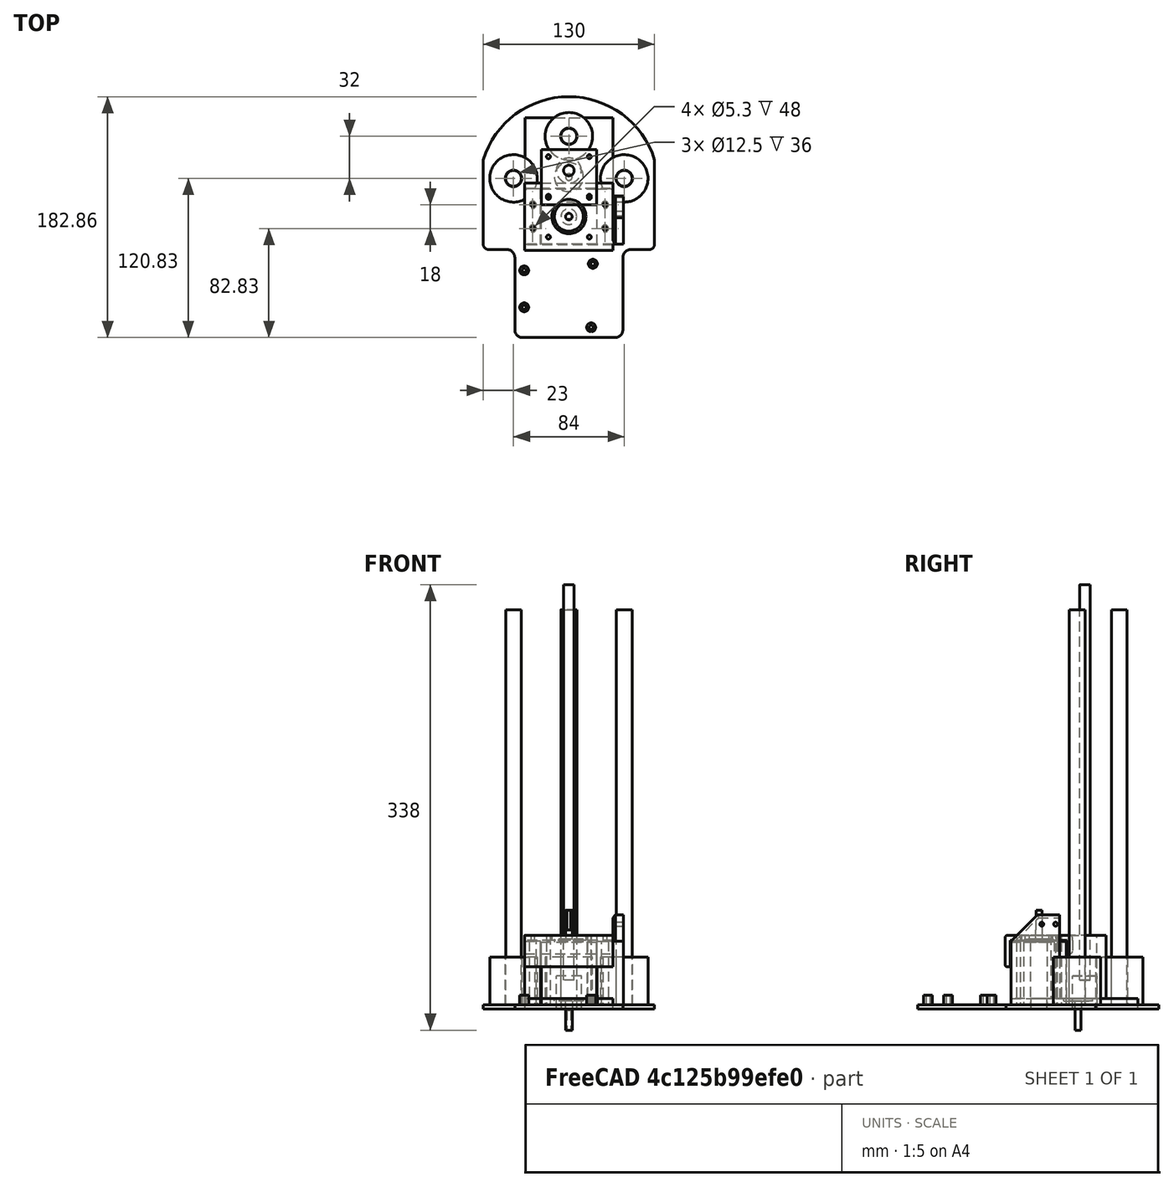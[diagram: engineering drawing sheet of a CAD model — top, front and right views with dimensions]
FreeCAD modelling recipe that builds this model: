
FCSTD DOCUMENT  (FreeCAD 0.18R16110 (Git))
Label: jSCARA-V3
License: All rights reserved
LicenseURL: http://en.wikipedia.org/wiki/All_rights_reserved
objects: PartDesign::Pad×15, Sketcher::SketchObject×10, Part::Cylinder×5, PartDesign::Fillet×4, PartDesign::Body×3, App::Part×3, PartDesign::Mirrored×2, Part::FeaturePython×2, Mesh::Feature×2, PartDesign::Chamfer×2, PartDesign::Pocket×1
note: 60 computed .brp shape members not serialized (recipe doc carries the construction recipe); baked Part::Feature solids carry a one-line shape summary decoded from their .brp

FEATURE [Sketcher::SketchObject] Sketch
  MapMode = 5
  Support = -> [XY_Plane]
  sketch-geometry (6):
    g0: LineSegment StartX=-65 StartY=-1.5e-15 StartZ=0 EndX=-65 EndY=-60 EndZ=0
    g1: LineSegment StartX=-65 StartY=-60 StartZ=0 EndX=65 EndY=-60 EndZ=0
    g2: LineSegment StartX=65 StartY=-60 StartZ=0 EndX=65 EndY=0 EndZ=0
    g3: ArcOfCircle CenterX=-1.086e-13 CenterY=-11.975 CenterZ=0 NormalX=0 NormalY=0 NormalZ=1 AngleXU=0 Radius=68 StartAngle=0.298147 EndAngle=2.84345
    g4: LineSegment StartX=65 StartY=8 StartZ=0 EndX=65 EndY=0 EndZ=0
    g5: LineSegment StartX=-65 StartY=-1.5e-15 StartZ=0 EndX=-65 EndY=8 EndZ=0
  constraints (18):
    c: Coincident(g0,g1)
    c: Coincident(g1,g2)
    c: Vertical(g2)
    c: Vertical(g0)
    c: Symmetric(g1,g0,g-2)
    c: DistanceX(g1,g1) = 130
    c: Equal(g0,g2)
    c: DistanceY(g2,g2) = 60
    c: Radius(g3) = 68
    c: Coincident(g4,g3)
    c: PointOnObject(g4,g-1)
    c: Vertical(g4)
    c: Coincident(g2,g4)
    c: Coincident(g5,g0)
    c: Coincident(g5,g3)
    c: Vertical(g5)
    c: Equal(g4,g5)
    c: DistanceY(g5,g5) = 8
FEATURE [PartDesign::Pad] Pad  label="Base"
  Length = 3.4
  Length2 = 100
  Profile = -> Sketch
  Type = 0
FEATURE [Part::Cylinder] Cylinder  label="R Rail"
  Angle = 360
  AttacherType = Attacher::AttachEngine3D
  Height = 300
  Placement = pos=(42,-6,3) rot=(0,0,1;0rad)
  Radius = 6
FEATURE [Sketcher::SketchObject] Sketch001
  MapMode = 5
  Placement = pos=(0,0,3.4) rot=(0,0,1;0rad)
  Support = -> [Pad]
  sketch-geometry (2):
    g0: Circle CenterX=42 CenterY=-6 CenterZ=0 NormalX=0 NormalY=0 NormalZ=1 AngleXU=0 Radius=6.25
    g1: Circle CenterX=42 CenterY=-6 CenterZ=0 NormalX=0 NormalY=0 NormalZ=1 AngleXU=0 Radius=18
  constraints (5):
    c: Radius(g0) = 6.25
    c: Coincident(g1,g0)
    c: Radius(g1) = 18
    c: DistanceY(g0,g-1) = 6
    c: DistanceX(g-1,g0) = 42
FEATURE [PartDesign::Fillet] Fillet
  Base = -> Pad [Edge5,Edge2]
  BaseFeature = -> Pad
  Radius = 4
FEATURE [PartDesign::Pad] Pad001  label="Rod Holder R"
  BaseFeature = -> Fillet
  Length = 36
  Length2 = 100
  Profile = -> Sketch001
  Type = 0
FEATURE [PartDesign::Mirrored] Mirrored  label="Rod Holder L"
  BaseFeature = -> Pad001
  MirrorPlane = -> YZ_Plane
  Originals = -> [Pad001]
FEATURE [Part::FeaturePython] b_NEMASteppper__42x48__001_  label="NEMASteppper (42x48)_001"  # a2plus imported part (geometry in sourceFile) (typed FeaturePython)
  Placement = pos=(0,-35,3) rot=(0,0,1;0rad)
  a2p_Version = V0.1
  fixedPosition = true
  sourceFile = .\NEMASteppper (42x48).FCStd
  subassemblyImport = false
  timeLastImport = 1.55797e+09
  updateColors = true
FEATURE [Part::Cylinder] Cylinder001  label="L Rail"
  Angle = 360
  AttacherType = Attacher::AttachEngine3D
  Height = 300
  Placement = pos=(-42,-6,3) rot=(0,0,1;0rad)
  Radius = 6
FEATURE [Sketcher::SketchObject] Sketch002
  MapMode = 5
  Placement = pos=(0,0,3.4) rot=(0,0,1;0rad)
  Support = -> [Mirrored]
  sketch-geometry (7):
    g0: LineSegment StartX=-21.4 StartY=-56 StartZ=0 EndX=-21.4 EndY=-14 EndZ=0
    g1: LineSegment StartX=-21.4 StartY=-14 StartZ=0 EndX=-33.4 EndY=-14 EndZ=0
    g2: LineSegment StartX=-33.4 StartY=-14 StartZ=0 EndX=-33.4 EndY=-56 EndZ=0
    g3: LineSegment StartX=-33.4 StartY=-56 StartZ=0 EndX=-21.4 EndY=-56 EndZ=0
    g4: Circle CenterX=-27.4 CenterY=-26 CenterZ=0 NormalX=0 NormalY=0 NormalZ=1 AngleXU=0 Radius=2.65
    g5: Circle CenterX=-27.4 CenterY=-44 CenterZ=0 NormalX=0 NormalY=0 NormalZ=1 AngleXU=0 Radius=2.65
    g6: LineSegment [constr] StartX=-27.4 StartY=-14 StartZ=0 EndX=-27.4 EndY=-56 EndZ=0
  constraints (21):
    c: Vertical(g0)
    c: Coincident(g0,g1)
    c: Horizontal(g1)
    c: Coincident(g1,g2)
    c: Vertical(g2)
    c: Coincident(g2,g3)
    c: Coincident(g3,g0)
    c: Horizontal(g3)
    c: DistanceY(g0,g-1) = 14
    c: DistanceY(g0,g0) = 42
    c: DistanceX(g1,g1) = 12
    c: DistanceX(g0,g-1) = 21.4
    c: DistanceY(g4,g1) = 12
    c: Equal(g4,g5) = 3
    c: PointOnObject(g6,g1)
    c: Symmetric(g0,g2,g6)
    c: PointOnObject(g5,g6)
    c: PointOnObject(g4,g6)
    c: PointOnObject(g6,g3)
    c: DistanceY(g2,g5) = 12
    c: Diameter(g4) = 5.3
FEATURE [PartDesign::Pad] Pad002
  BaseFeature = -> Mirrored
  Length = 48
  Length2 = 100
  Profile = -> Sketch002
  Type = 0
FEATURE [PartDesign::Mirrored] Mirrored001
  BaseFeature = -> Pad002
  MirrorPlane = -> Sketch002 [V_Axis]
  Originals = -> [Pad002]
FEATURE [Sketcher::SketchObject] Sketch003
  MapMode = 5
  Support = -> [XY_Plane002]
  sketch-geometry (14):
    g0: Circle CenterX=-27.4 CenterY=-26 CenterZ=0 NormalX=0 NormalY=0 NormalZ=1 AngleXU=0 Radius=1.5
    g1: Circle CenterX=0 CenterY=-35 CenterZ=0 NormalX=0 NormalY=0 NormalZ=1 AngleXU=0 Radius=13
    g2: LineSegment StartX=-33.4 StartY=-14 StartZ=0 EndX=33.4 EndY=-14 EndZ=0
    g3: LineSegment StartX=33.4 StartY=-14 StartZ=0 EndX=33.4 EndY=-56 EndZ=0
    g4: LineSegment StartX=33.4 StartY=-56 StartZ=0 EndX=-33.4 EndY=-56 EndZ=0
    g5: LineSegment StartX=-33.4 StartY=-56 StartZ=0 EndX=-33.4 EndY=-14 EndZ=0
    g6: Circle CenterX=27.4 CenterY=-26 CenterZ=0 NormalX=0 NormalY=0 NormalZ=1 AngleXU=0 Radius=1.5
    g7: Circle CenterX=27.4 CenterY=-44 CenterZ=0 NormalX=0 NormalY=0 NormalZ=1 AngleXU=0 Radius=1.5
    g8: Circle CenterX=-27.4 CenterY=-44 CenterZ=0 NormalX=0 NormalY=0 NormalZ=1 AngleXU=0 Radius=1.5
    g9: LineSegment [constr] StartX=-27.4 StartY=-26 StartZ=0 EndX=-27.4 EndY=-44 EndZ=0
    g10: Circle CenterX=-15.5 CenterY=-50.5 CenterZ=0 NormalX=0 NormalY=0 NormalZ=1 AngleXU=0 Radius=1.5
    g11: Circle CenterX=15.5 CenterY=-50.5 CenterZ=0 NormalX=0 NormalY=0 NormalZ=1 AngleXU=0 Radius=1.5
    g12: Circle CenterX=-15.5 CenterY=-19.5 CenterZ=0 NormalX=0 NormalY=0 NormalZ=1 AngleXU=0 Radius=1.5
    g13: Circle CenterX=15.5 CenterY=-19.5 CenterZ=0 NormalX=0 NormalY=0 NormalZ=1 AngleXU=0 Radius=1.5
  constraints (36):
    c: PointOnObject(g1,g-2)
    c: Radius(g1) = 13
    c: DistanceY(g1,g-1) = 35
    c: Coincident(g2,g3)
    c: Coincident(g3,g4)
    c: Coincident(g4,g5)
    c: Coincident(g5,g2)
    c: Horizontal(g4)
    c: Vertical(g3)
    c: Vertical(g5)
    c: DistanceX(g2,g2) = 66.8
    c: Symmetric(g2,g2,g-2)
    c: DistanceY(g3,g3) = 42
    c: DistanceY(g2,g-1) = 14
    c: Equal(g0,g6) = 3
    c: Symmetric(g6,g0,g-2)
    c: Equal(g0,g8) = 3
    c: Equal(g8,g7) = 3
    c: DistanceY(g1,g6) = 9
    c: DistanceY(g8,g0) = 18
    c: Symmetric(g7,g8,g-2)
    c: Coincident(g9,g0)
    c: Coincident(g9,g8)
    c: Vertical(g9)
    c: Radius(g10) = 1.5
    c: Equal(g10,g11) = 3
    c: Symmetric(g10,g11,g-2)
    c: DistanceX(g10,g11) = 31
    c: DistanceY(g3,g11) = 5.5
    c: Equal(g10,g12) = 3
    c: Symmetric(g12,g13,g-2)
    c: DistanceX(g12,g13) = 31
    c: DistanceY(g10,g12) = 31
    c: Equal(g13,g12)
    c: DistanceX(g4,g8) = 6
    c: Radius(g0) = 1.5
FEATURE [PartDesign::Pad] Pad003
  Length = 4
  Length2 = 100
  Profile = -> Sketch003
  Type = 0
FEATURE [PartDesign::Fillet] Fillet002
  Base = -> Mirrored001 [Edge43,Edge56]
  BaseFeature = -> Mirrored001
  Radius = 2
FEATURE [PartDesign::Pad] Pad004
  BaseFeature = -> Pad003
  Length = 0.6
  Length2 = 100
  Profile = -> Pad003 [Face3]
  Type = 0
FEATURE [PartDesign::Pad] Pad005
  BaseFeature = -> Pad004
  Length = 4
  Length2 = 100
  Profile = -> Pad004 [Face19]
  Type = 0
FEATURE [PartDesign::Pad] Pad006
  BaseFeature = -> Pad005
  Length = 20
  Length2 = 100
  Profile = -> Pad005 [Face21]
  Type = 0
FEATURE [PartDesign::Pad] Pad007
  BaseFeature = -> Pad006
  Length = 0.6
  Length2 = 100
  Profile = -> Pad006 [Face1]
  Type = 0
FEATURE [PartDesign::Pad] Pad008
  BaseFeature = -> Pad007
  Length = 4
  Length2 = 100
  Profile = -> Pad007 [Face11]
  Type = 0
FEATURE [PartDesign::Pad] Pad009
  BaseFeature = -> Pad008
  Length = 10
  Length2 = 100
  Profile = -> Pad008 [Face28]
  Type = 0
FEATURE [PartDesign::Fillet] Fillet003
  Base = -> Pad009 [Edge83,Edge65,Edge75,Edge87]
  BaseFeature = -> Pad009
  Radius = 2
FEATURE [PartDesign::Body] Body001  label="Stepper Retainer"
  Group = -> [Sketch003,Pad003,Pad004,Pad005,Pad006,Pad007,Pad008,Pad009,Fillet003]
  Origin = -> Origin002
  Placement = pos=(0,0,52) rot=(0,0,1;0rad)
  Tip = -> Fillet003
FEATURE [Mesh::Feature] KW12_3_Microswitch  label="KW12-3 Microswitch"
  Placement = pos=(48,-15,58) rot=(-0.57735,0.57735,0.57735;4.18879rad)
FEATURE [Part::Cylinder] Cylinder002  label="Lead Screw Coupler"
  Angle = 360
  AttacherType = Attacher::AttachEngine3D
  Height = 25
  Radius = 9.5
FEATURE [Sketcher::SketchObject] Sketch004
  ExternalGeometry = -> [Fillet002]
  MapMode = 5
  Placement = pos=(0,0,3.4) rot=(0,0,1;0rad)
  Support = -> [Fillet002]
  sketch-geometry (4):
    g0: LineSegment StartX=33.4 StartY=-19.3196 StartZ=0 EndX=41.4 EndY=-19.3196 EndZ=0
    g1: LineSegment StartX=41.4 StartY=-19.3196 StartZ=0 EndX=41.4 EndY=-56 EndZ=0
    g2: LineSegment StartX=41.4 StartY=-56 StartZ=0 EndX=33.4 EndY=-56 EndZ=0
    g3: LineSegment StartX=33.4 StartY=-56 StartZ=0 EndX=33.4 EndY=-19.3196 EndZ=0
  constraints (9):
    c: Coincident(g0,g1)
    c: Coincident(g1,g2)
    c: Coincident(g2,g3)
    c: Coincident(g3,g0)
    c: Horizontal(g0)
    c: Horizontal(g2)
    c: Vertical(g1)
    c: Vertical(g3)
    c: DistanceX(g0,g0) = 8
FEATURE [PartDesign::Pad] Pad010
  BaseFeature = -> Fillet002
  Length = 68
  Length2 = 100
  Profile = -> Sketch004
  Type = 0
FEATURE [PartDesign::Chamfer] Chamfer
  Base = -> Pad010 [Edge78]
  BaseFeature = -> Pad010
  Size = 20
FEATURE [PartDesign::Chamfer] Chamfer001
  Base = -> Chamfer [Edge12,Edge35]
  BaseFeature = -> Chamfer
  Size = 2
FEATURE [Sketcher::SketchObject] Sketch005
  MapMode = 5
  Placement = pos=(41.4,0,0) rot=(0.57735,0.57735,0.57735;2.0944rad)
  Support = -> [Chamfer001]
  sketch-geometry (3):
    g0: Circle CenterX=-32.7462 CenterY=64.4514 CenterZ=0 NormalX=0 NormalY=0 NormalZ=1 AngleXU=0 Radius=1.5
    g1: Circle CenterX=-22.2462 CenterY=64.4514 CenterZ=0 NormalX=0 NormalY=0 NormalZ=1 AngleXU=0 Radius=1.5
    g2: LineSegment [constr] StartX=-32.7462 StartY=64.4514 StartZ=0 EndX=-22.2462 EndY=64.4514 EndZ=0
  constraints (6):
    c: Radius(g0) = 1.5
    c: Horizontal(g2)
    c: Coincident(g2,g0)
    c: Coincident(g2,g1)
    c: Equal(g1,g0)
    c: DistanceX(g2,g2) = 10.5
FEATURE [PartDesign::Pocket] Pocket
  BaseFeature = -> Chamfer001
  Length = 10
  Length2 = 0
  Profile = -> Sketch005
  Type = 0
FEATURE [Part::Cylinder] Cylinder003  label="Lead Screw"
  Angle = 360
  AttacherType = Attacher::AttachEngine3D
  Height = 300
  Placement = pos=(0,0,22) rot=(0,0,1;0rad)
  Radius = 4
FEATURE [App::Part] Part001  label="Z Screw"
  Group = -> [Cylinder003,Cylinder002]
  Origin = -> Origin003
  Placement = pos=(0,-35,61) rot=(0,0,1;0rad)
FEATURE [Sketcher::SketchObject] Sketch006
  MapMode = 5
  Support = -> [XY_Plane005]
  sketch-geometry (5):
    g0: LineSegment StartX=-33.3207 StartY=40 StartZ=0 EndX=33.3207 EndY=40 EndZ=0
    g1: LineSegment StartX=33.3207 StartY=40 StartZ=0 EndX=33.3207 EndY=-56 EndZ=0
    g2: LineSegment StartX=33.3207 StartY=-56 StartZ=0 EndX=-33.3207 EndY=-56 EndZ=0
    g3: LineSegment StartX=-33.3207 StartY=-56 StartZ=0 EndX=-33.3207 EndY=40 EndZ=0
    g4: Circle CenterX=0 CenterY=-35.0087 CenterZ=0 NormalX=0 NormalY=0 NormalZ=1 AngleXU=0 Radius=6
  constraints (12):
    c: Coincident(g0,g1)
    c: Coincident(g1,g2)
    c: Coincident(g2,g3)
    c: Coincident(g3,g0)
    c: Horizontal(g2)
    c: Vertical(g1)
    c: Vertical(g3)
    c: Symmetric(g0,g0,g-2)
    c: DistanceY(g2,g-1) = 56
    c: DistanceY(g-1,g0) = 40
    c: Radius(g4) = 6
    c: PointOnObject(g4,g-2)
FEATURE [PartDesign::Pad] Pad011
  Length = 8
  Length2 = 100
  Profile = -> Sketch006
  Type = 0
FEATURE [PartDesign::Body] Body002
  Group = -> [Sketch006,Pad011]
  Origin = -> Origin005
  Tip = -> Pad011
FEATURE [Part::FeaturePython] b_NEMASteppper__42x48__001_001  label="NEMASteppper (42x48)_002"  # a2plus imported part (geometry in sourceFile) (typed FeaturePython)
  Placement = pos=(0,-5,56) rot=(1,0,0;3.14159rad)
  a2p_Version = V0.1
  fixedPosition = true
  sourceFile = .\NEMASteppper (42x48).FCStd
  subassemblyImport = false
  timeLastImport = 1.55797e+09
  updateColors = true
FEATURE [App::Part] Part002  label="Carriage"
  Group = -> [Body002,b_NEMASteppper__42x48__001_001]
  Origin = -> Origin004
  Placement = pos=(0,0,120) rot=(0,0,1;0rad)
FEATURE [Part::Cylinder] Cylinder004  label="Front Rail"
  Angle = 360
  AttacherType = Attacher::AttachEngine3D
  Height = 300
  Placement = pos=(0,26,3) rot=(0,0,1;0rad)
  Radius = 6
FEATURE [Sketcher::SketchObject] Sketch007
  MapMode = 5
  Placement = pos=(0,0,3.4) rot=(0,0,1;0rad)
  Support = -> [Pocket]
  sketch-geometry (2):
    g0: Circle CenterX=0 CenterY=26 CenterZ=0 NormalX=0 NormalY=0 NormalZ=1 AngleXU=0 Radius=6.25
    g1: Circle CenterX=0 CenterY=26 CenterZ=0 NormalX=0 NormalY=0 NormalZ=1 AngleXU=0 Radius=18
  constraints (5):
    c: Radius(g0) = 6.25
    c: DistanceY(g-1,g0) = 26
    c: PointOnObject(g0,g-2)
    c: Radius(g1) = 18
    c: Coincident(g0,g1)
FEATURE [PartDesign::Pad] Pad012
  BaseFeature = -> Pocket
  Length = 36
  Length2 = 100
  Profile = -> Sketch007
  Type = 0
FEATURE [Mesh::Feature] Arduino_ipt  label="Arduino.ipt"
  Placement = pos=(6,-60,42) rot=(0,0,1;1.5708rad)
FEATURE [Sketcher::SketchObject] Sketch008
  ExternalGeometry = -> [Pad012]
  MapMode = 5
  Support = -> [XY_Plane]
  sketch-geometry (4):
    g0: LineSegment StartX=-41.0016 StartY=-60 StartZ=0 EndX=41.0016 EndY=-60 EndZ=0
    g1: LineSegment StartX=41.0016 StartY=-60 StartZ=0 EndX=41.0016 EndY=-126.827 EndZ=0
    g2: LineSegment StartX=41.0016 StartY=-126.827 StartZ=0 EndX=-41.0016 EndY=-126.827 EndZ=0
    g3: LineSegment StartX=-41.0016 StartY=-126.827 StartZ=0 EndX=-41.0016 EndY=-60 EndZ=0
  constraints (9):
    c: Coincident(g0,g1)
    c: Coincident(g1,g2)
    c: Coincident(g2,g3)
    c: Coincident(g3,g0)
    c: Horizontal(g0)
    c: Vertical(g1)
    c: Vertical(g3)
    c: PointOnObject(g0,g-3)
    c: Symmetric(g1,g2,g-2)
FEATURE [PartDesign::Pad] Pad013
  BaseFeature = -> Pad012
  Length = 3.4
  Length2 = 100
  Profile = -> Sketch008
  Type = 0
FEATURE [Sketcher::SketchObject] Sketch009
  MapMode = 5
  Placement = pos=(0,0,3.4) rot=(0,0,1;0rad)
  Support = -> [Pad013]
  sketch-geometry (8):
    g0: Circle CenterX=16.9 CenterY=-119 CenterZ=0 NormalX=0 NormalY=0 NormalZ=1 AngleXU=0 Radius=1.5
    g1: Circle CenterX=16.9 CenterY=-119 CenterZ=0 NormalX=0 NormalY=0 NormalZ=1 AngleXU=0 Radius=3.4
    g2: Circle CenterX=-33.9 CenterY=-103.8 CenterZ=0 NormalX=0 NormalY=0 NormalZ=1 AngleXU=0 Radius=1.5
    g3: Circle CenterX=-33.9 CenterY=-103.8 CenterZ=0 NormalX=0 NormalY=0 NormalZ=1 AngleXU=0 Radius=3.4
    g4: Circle CenterX=-33.9 CenterY=-75.8 CenterZ=0 NormalX=0 NormalY=0 NormalZ=1 AngleXU=0 Radius=3.4
    g5: Circle CenterX=-33.9 CenterY=-75.8 CenterZ=0 NormalX=0 NormalY=0 NormalZ=1 AngleXU=0 Radius=1.5
    g6: Circle CenterX=18.2 CenterY=-70.8 CenterZ=0 NormalX=0 NormalY=0 NormalZ=1 AngleXU=0 Radius=1.5
    g7: Circle CenterX=18.2 CenterY=-70.8 CenterZ=0 NormalX=0 NormalY=0 NormalZ=1 AngleXU=0 Radius=3.4
  constraints (16):
    c: Radius(g0) = 1.5
    c: DistanceX(g0) = 16.9
    c: DistanceY(g0) = -119
    c: Coincident(g1,g0)
    c: Radius(g1) = 3.4
    c: Equal(g0,g2) = 1.5
    c: Coincident(g3,g2)
    c: Equal(g1,g3) = 3.4
    c: DistanceX(g2,g0) = 50.8
    c: Coincident(g4,g5)
    c: DistanceY(g0,g2) = 15.2
    c: DistanceX(g2,g4) = 0
    c: DistanceY(g2,g4) = 28
    c: Coincident(g7,g6)
    c: DistanceX(g4,g6) = 52.1
    c: DistanceY(g4,g6) = 5
FEATURE [PartDesign::Pad] Pad014
  BaseFeature = -> Pad013
  Length = 7
  Length2 = 100
  Profile = -> Sketch009
  Type = 0
FEATURE [PartDesign::Fillet] Fillet004
  Base = -> Pad014 [Edge78,Edge88,Edge124,Edge126]
  BaseFeature = -> Pad014
  Radius = 6
FEATURE [PartDesign::Body] Body  label="Base Plate"
  Group = -> [Sketch,Pad,Sketch001,Fillet,Pad001,Mirrored,Sketch002,Pad002,Mirrored001,Fillet002,Sketch004,Pad010,Chamfer,Chamfer001,Sketch005,Pocket,Sketch007,Pad012,Sketch008,Pad013,Sketch009,Pad014,Fillet004]
  Origin = -> Origin
  Tip = -> Fillet004
FEATURE [App::Part] Part  label="Base Assembly"
  Group = -> [Cylinder001,Cylinder,Body,b_NEMASteppper__42x48__001_,Body001,KW12_3_Microswitch,Cylinder004,Arduino_ipt]
  Origin = -> Origin001
